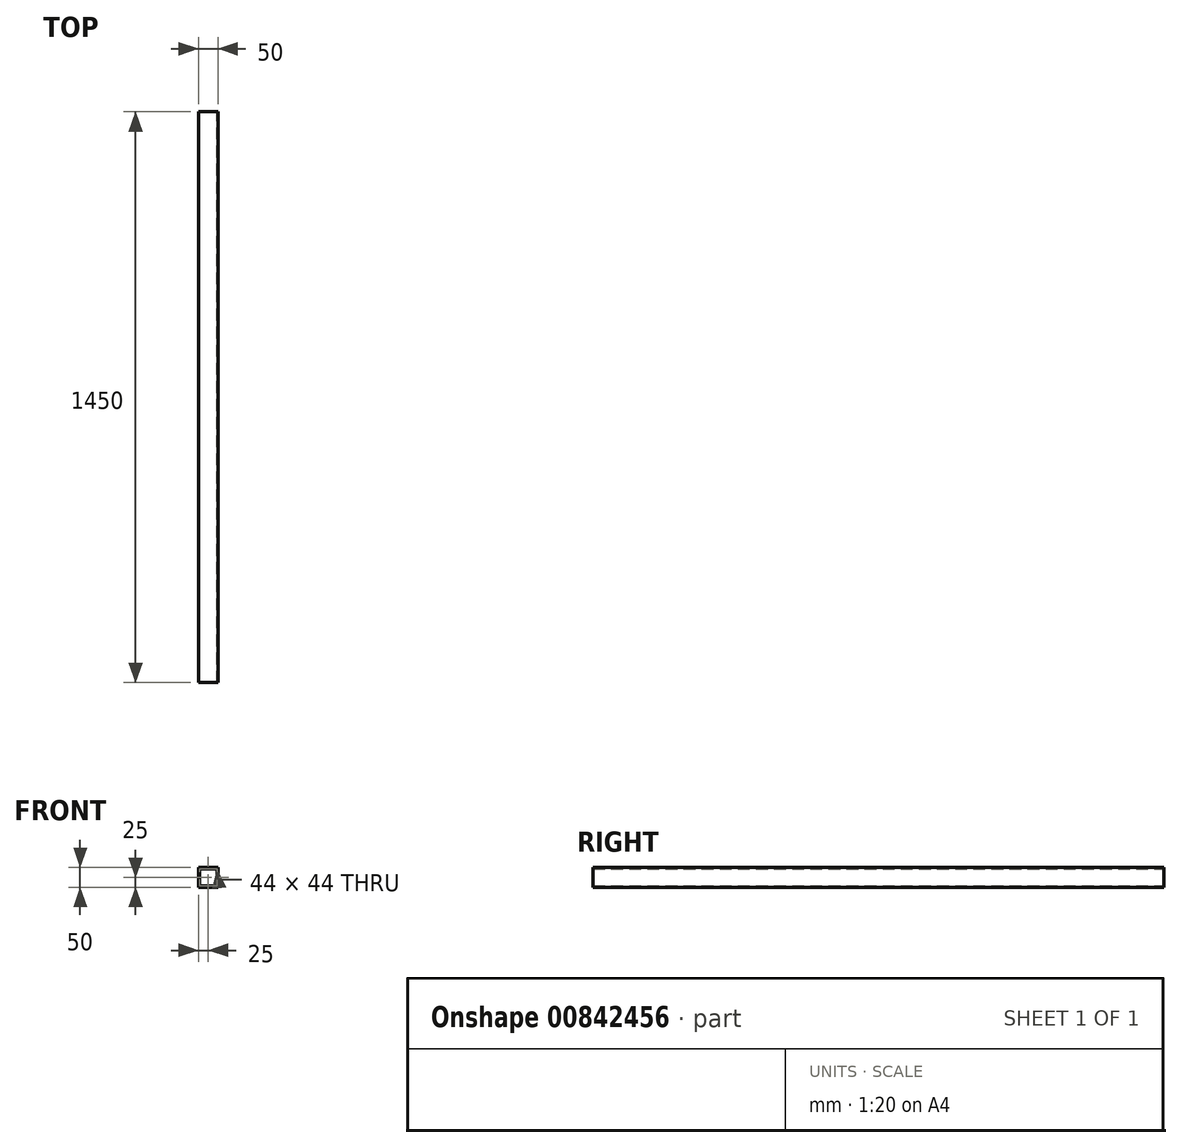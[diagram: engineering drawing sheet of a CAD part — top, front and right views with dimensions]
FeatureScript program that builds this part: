
annotation { "Feature Type Name" : "Feature", "Feature Type Description" : "" }
export const myFeature = defineFeature(function(context is Context, id is Id, definition is map)
    precondition{}
    {
        {
            var Q0;
            Q0=qCreatedBy(makeId("Front.planeOp"),FACE);
            var sketch = newSketch(context, id + "F0", { "sketchPlane" : qUnion([Q0])});
            skLineSegment(sketch, "E0.bottom", {"start": v(25, -25) * mm, "end": v(-25, -25) * mm});
            skLineSegment(sketch, "E0.top", {"start": v(25, 25) * mm, "end": v(-25, 25) * mm});
            skLineSegment(sketch, "E0.left", {"start": v(25, -25) * mm, "end": v(25, 25) * mm});
            skLineSegment(sketch, "E0.right", {"start": v(-25, -25) * mm, "end": v(-25, 25) * mm});
            skPoint(sketch, "E0.middle", {"position": v(0, 0) * mm});
            skLineSegment(sketch, "E1.0", {"start": v(22, 22) * mm, "end": v(-22, 22) * mm});
            skLineSegment(sketch, "E1.1", {"start": v(22, -22) * mm, "end": v(22, 22) * mm});
            skLineSegment(sketch, "E1.2", {"start": v(22, -22) * mm, "end": v(-22, -22) * mm});
            skLineSegment(sketch, "E1.3", {"start": v(-22, -22) * mm, "end": v(-22, 22) * mm});
            skSolve(sketch);
        }
        {
            var Q0;
            Q0=makeQuery(id+"F0.imprint","IMPRINT",FACE,{"disambiguationData":[TD([[makeQuery(id+"F0.imprint","IMPRINT",EDGE,{"derivedFrom":sQuery(id+"F0.wireOp",EDGE,"E0.bottom")}),-1.0]])]});
            extrude(context, id + "F1", {"entities" : qUnion([Q0]), "depth" : 1450 * mm, "offsetDistance" : 25 * mm});
        }
    });
